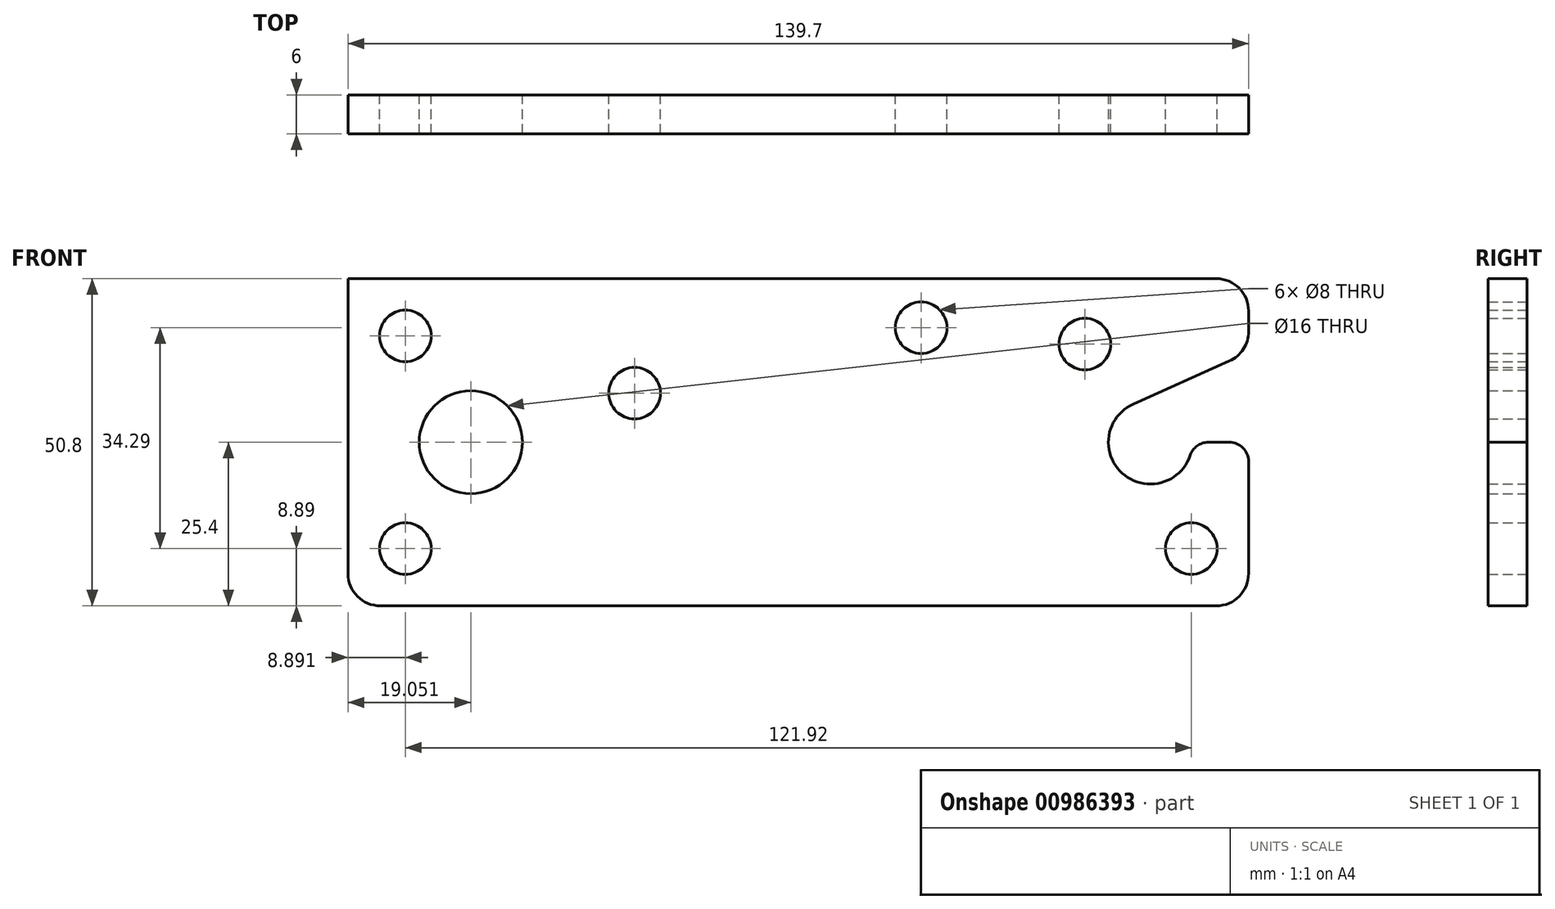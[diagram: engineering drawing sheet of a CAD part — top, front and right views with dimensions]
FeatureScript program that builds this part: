
annotation { "Feature Type Name" : "Feature", "Feature Type Description" : "" }
export const myFeature = defineFeature(function(context is Context, id is Id, definition is map)
    precondition{}
    {
        {
            var Q0;
            Q0=qCreatedBy(makeId("Front.planeOp"),FACE);
            var sketch = newSketch(context, id + "F0", { "sketchPlane" : qUnion([Q0])});
            skLineSegment(sketch, "E0", {"start": v(-67.05, 0) * mm, "end": v(72.65, 0) * mm});
            skLineSegment(sketch, "E1", {"start": v(-67.05, 0) * mm, "end": v(-67.05, 50.8) * mm});
            skLineSegment(sketch, "E2", {"start": v(72.65, 0) * mm, "end": v(72.65, 25.4) * mm});
            skArc(sketch, "E3", {"start": v(50.91, 25.4) * mm, "mid": v(57.41, 18.9) * mm, "end": v(63.91, 25.4) * mm});
            skPoint(sketch, "E4.end.orphan", {"position": v(61.33, 8.89) * mm});
            skCircle(sketch, "E5", {"center": v(63.76, 8.89) * mm, "radius": 4 * mm});
            skPoint(sketch, "E6.orphan", {"position": v(72.65, 8.89) * mm});
            skLineSegment(sketch, "E7", {"start": v(-67.05, 0) * mm, "end": v(-67.05, 8.9) * mm});
            skCircle(sketch, "E8", {"center": v(-58.16, 8.9) * mm, "radius": 4 * mm});
            skLineSegment(sketch, "E9", {"start": v(-67.05, 50.8) * mm, "end": v(-67.05, 41.9) * mm});
            skCircle(sketch, "E10", {"center": v(-58.16, 41.9) * mm, "radius": 4 * mm});
            skCircle(sketch, "E11", {"center": v(-48, 25.4) * mm, "radius": 8 * mm});
            skPoint(sketch, "E12.orphan", {"position": v(-67.05, 25.4) * mm});
            skLineSegment(sketch, "E13", {"start": v(-67.05, 50.8) * mm, "end": v(72.65, 50.8) * mm});
            skLineSegment(sketch, "E14", {"start": v(72.65, 50.8) * mm, "end": v(72.65, 39.35) * mm});
            skArc(sketch, "E15", {"start": v(54.75, 31.33) * mm, "mid": v(53.88, 19.94) * mm, "end": v(63.91, 25.4) * mm});
            skLineSegment(sketch, "E16", {"start": v(72.65, 50.8) * mm, "end": v(47.25, 50.8) * mm});
            skCircle(sketch, "E17", {"center": v(47.25, 40.64) * mm, "radius": 4 * mm});
            skLineSegment(sketch, "E18", {"start": v(72.65, 50.8) * mm, "end": v(21.85, 50.8) * mm});
            skCircle(sketch, "E19", {"center": v(21.85, 43.18) * mm, "radius": 4 * mm});
            skLineSegment(sketch, "E20", {"start": v(-67.05, 50.8) * mm, "end": v(-22.6, 50.8) * mm});
            skCircle(sketch, "E21", {"center": v(-22.6, 33.02) * mm, "radius": 4 * mm});
            skLineSegment(sketch, "E22", {"start": v(72.65, 39.35) * mm, "end": v(54.75, 31.33) * mm});
            skLineSegment(sketch, "E23", {"start": v(72.65, 25.4) * mm, "end": v(63.91, 25.4) * mm});
            skSolve(sketch);
        }
        {
            var Q0;
            Q0=qSketchRegion(id+"F0",true);
            extrude(context, id + "F1", {"entities" : qUnion([Q0]), "depth" : 6 * mm, "offsetDistance" : 25 * mm});
        }
        {
            var Q0;
            Q0=makeQuery(id+"F1.opExtrude","SWEPT_EDGE",EDGE,{"disambiguationData":[OSD([sQuery(id+"F0.wireOp",EDGE,"WXCflpe4-IZAw-97a0-CYCy-0BuLOTbjZ9ix"),sQuery(id+"F0.wireOp",EDGE,"E9")])]});
            var Q1;
            Q1=makeQuery(id+"F1.opExtrude","SWEPT_EDGE",EDGE,{"disambiguationData":[OSD([sQuery(id+"F0.wireOp",EDGE,"E0"),sQuery(id+"F0.wireOp",EDGE,"E7")])]});
            var Q2;
            Q2=makeQuery(id+"F1.opExtrude","SWEPT_EDGE",EDGE,{"disambiguationData":[OSD([sQuery(id+"F0.wireOp",EDGE,"E0"),sQuery(id+"F0.wireOp",EDGE,"E2")])]});
            fillet(context, id + "F2", {"entities" : qUnion([Q0, Q1, Q2]), "radius" : 5 * mm, "tangentPropagation" : true, "allowEdgeOverflow" : false});
        }
        {
            var Q0;
            Q0=makeQuery(id+"F1.opExtrude","SWEPT_EDGE",EDGE,{"disambiguationData":[OSD([sQuery(id+"F0.wireOp",EDGE,"E18"),sQuery(id+"F0.wireOp",EDGE,"E14")])]});
            fillet(context, id + "F3", {"entities" : qUnion([Q0]), "radius" : 5 * mm, "tangentPropagation" : true, "allowEdgeOverflow" : false});
        }
        {
            var Q0;
            Q0=makeQuery(id+"F1.opExtrude","SWEPT_EDGE",EDGE,{"disambiguationData":[OSD([sQuery(id+"F0.wireOp",EDGE,"E15"),sQuery(id+"F0.wireOp",EDGE,"E23")])]});
            fillet(context, id + "F4", {"entities" : qUnion([Q0]), "radius" : 3 * mm, "tangentPropagation" : true, "allowEdgeOverflow" : false});
        }
    });
